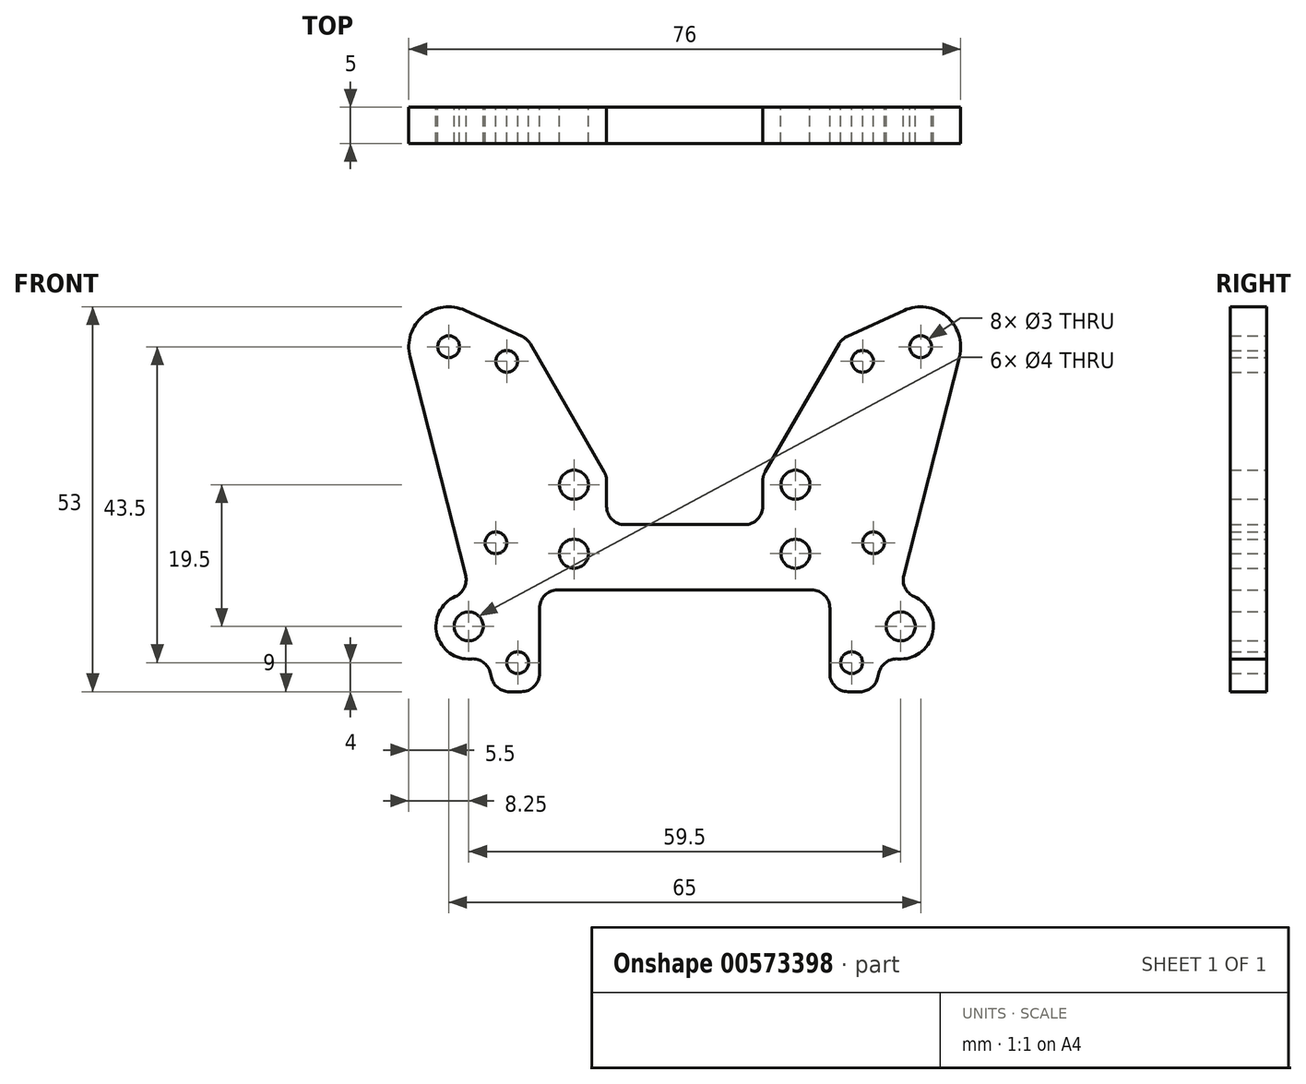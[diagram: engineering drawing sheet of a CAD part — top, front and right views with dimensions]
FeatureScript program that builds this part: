
annotation { "Feature Type Name" : "Feature", "Feature Type Description" : "" }
export const myFeature = defineFeature(function(context is Context, id is Id, definition is map)
    precondition{}
    {
        {
            var Q0;
            Q0=qCreatedBy(makeId("Front.planeOp"),FACE);
            var sketch = newSketch(context, id + "F0", { "sketchPlane" : qUnion([Q0])});
            skLineSegment(sketch, "E0", {"start": v(0, 78.36) * mm, "end": v(0, -63.42) * mm, "construction": true});
            skCircle(sketch, "E1", {"center": v(23, -10) * mm, "radius": 1.5 * mm});
            skCircle(sketch, "E2", {"center": v(29.75, -5) * mm, "radius": 2 * mm});
            skCircle(sketch, "E3", {"center": v(26, 6.5) * mm, "radius": 1.5 * mm});
            skCircle(sketch, "E4", {"center": v(15.25, 5) * mm, "radius": 2 * mm});
            skCircle(sketch, "E5", {"center": v(15.25, 14.5) * mm, "radius": 2 * mm});
            skCircle(sketch, "E6", {"center": v(24.5, 31.5) * mm, "radius": 1.5 * mm});
            skCircle(sketch, "E7", {"center": v(32.5, 33.5) * mm, "radius": 1.5 * mm});
            skLineSegment(sketch, "E8", {"start": v(22.5, -14) * mm, "end": v(24.17, -14) * mm});
            skLineSegment(sketch, "E9", {"start": v(26.59, -12.12) * mm, "end": v(26.78, -11.36) * mm});
            skArc(sketch, "E10.0", {"start": v(29.4, -9.49) * mm, "mid": v(34.11, -6.1) * mm, "end": v(31.58, -0.89) * mm});
            skLineSegment(sketch, "E11.trimOffspring", {"start": v(30.18, 2) * mm, "end": v(37.83, 32.15) * mm});
            skPoint(sketch, "E12.visualSharp", {"position": v(26.11, -14) * mm});
            skArc(sketch, "E12.filletArc", {"start": v(24.17, -14) * mm, "mid": v(25.7, -13.47) * mm, "end": v(26.59, -12.12) * mm});
            skArc(sketch, "E13.0", {"start": v(37.83, 32.15) * mm, "mid": v(36.03, 37.72) * mm, "end": v(30.22, 38.5) * mm});
            skLineSegment(sketch, "E14", {"start": v(30.22, 38.5) * mm, "end": v(22.4, 34.94) * mm});
            skLineSegment(sketch, "E15", {"start": v(10.75, 15.04) * mm, "end": v(10.75, 11.5) * mm});
            skLineSegment(sketch, "E16", {"start": v(8.25, 9) * mm, "end": v(0, 9) * mm});
            skLineSegment(sketch, "E17", {"start": v(0, 9) * mm, "end": v(0, 0) * mm});
            skLineSegment(sketch, "E18", {"start": v(0, 0) * mm, "end": v(17.5, 0) * mm});
            skLineSegment(sketch, "E19", {"start": v(20, -2.5) * mm, "end": v(20, -11.5) * mm});
            skPoint(sketch, "E20.visualSharp", {"position": v(10.75, 29.63) * mm});
            skPoint(sketch, "E21.visualSharp", {"position": v(10.75, 9) * mm});
            skArc(sketch, "E21.filletArc", {"start": v(8.25, 9) * mm, "mid": v(10.02, 9.73) * mm, "end": v(10.75, 11.5) * mm});
            skPoint(sketch, "E22.visualSharp", {"position": v(20, 0) * mm});
            skArc(sketch, "E22.filletArc", {"start": v(20, -2.5) * mm, "mid": v(19.27, -0.73) * mm, "end": v(17.5, 0) * mm});
            skPoint(sketch, "E23.visualSharp", {"position": v(20, -14) * mm});
            skArc(sketch, "E23.filletArc", {"start": v(20, -11.5) * mm, "mid": v(20.73, -13.27) * mm, "end": v(22.5, -14) * mm});
            skLineSegment(sketch, "E24", {"start": v(11.09, 16.29) * mm, "end": v(21.28, 33.92) * mm});
            skPoint(sketch, "E25.visualSharp", {"position": v(21.68, 34.6) * mm});
            skArc(sketch, "E25.filletArc", {"start": v(22.4, 34.94) * mm, "mid": v(21.76, 34.52) * mm, "end": v(21.28, 33.92) * mm});
            skPoint(sketch, "E26.visualSharp", {"position": v(10.75, 15.7) * mm});
            skArc(sketch, "E26.filletArc", {"start": v(11.09, 16.29) * mm, "mid": v(10.84, 15.68) * mm, "end": v(10.75, 15.04) * mm});
            skLineSegment(sketch, "E27", {"start": v(23.2, 32.25) * mm, "end": v(13.52, 15.5) * mm, "construction": true});
            skPoint(sketch, "E28.visualSharp", {"position": v(29.54, -0.5) * mm});
            skArc(sketch, "E28.filletArc", {"start": v(30.18, 2) * mm, "mid": v(30.35, 0.3) * mm, "end": v(31.58, -0.89) * mm});
            skPoint(sketch, "E29.visualSharp", {"position": v(27.42, -8.85) * mm});
            skArc(sketch, "E29.filletArc", {"start": v(29.4, -9.49) * mm, "mid": v(27.75, -9.95) * mm, "end": v(26.78, -11.36) * mm});
            skSolve(sketch);
        }
        {
            var Q0;
            Q0=qSketchRegion(id+"F0",true);
            extrude(context, id + "F1", {"entities" : qUnion([Q0]), "depth" : 5 * mm});
        }
        {
            var Q0;
            Q0=makeQuery(id+"F1.opExtrude","SWEPT_BODY",BODY,{"disambiguationData":[OSD([sQuery(id+"F0.wireOp",EDGE,"E1"),sQuery(id+"F0.wireOp",EDGE,"E2"),sQuery(id+"F0.wireOp",EDGE,"E3"),sQuery(id+"F0.wireOp",EDGE,"E4"),sQuery(id+"F0.wireOp",EDGE,"E5"),sQuery(id+"F0.wireOp",EDGE,"E6"),sQuery(id+"F0.wireOp",EDGE,"E7"),sQuery(id+"F0.wireOp",EDGE,"E8"),sQuery(id+"F0.wireOp",EDGE,"E9"),sQuery(id+"F0.wireOp",EDGE,"E10.0"),sQuery(id+"F0.wireOp",EDGE,"E11.trimOffspring"),sQuery(id+"F0.wireOp",EDGE,"E12.filletArc"),sQuery(id+"F0.wireOp",EDGE,"E13.0"),sQuery(id+"F0.wireOp",EDGE,"E14"),sQuery(id+"F0.wireOp",EDGE,"E15"),sQuery(id+"F0.wireOp",EDGE,"E16"),sQuery(id+"F0.wireOp",EDGE,"E17"),sQuery(id+"F0.wireOp",EDGE,"E18"),sQuery(id+"F0.wireOp",EDGE,"E19"),sQuery(id+"F0.wireOp",EDGE,"E20.filletArc"),sQuery(id+"F0.wireOp",EDGE,"E21.filletArc"),sQuery(id+"F0.wireOp",EDGE,"E22.filletArc"),sQuery(id+"F0.wireOp",EDGE,"E23.filletArc")])]});
            var Q1;
            Q1=qCreatedBy(makeId("Right.planeOp"),FACE);
            mirror(context, id + "F2", {"operationType" : NewBodyOperationType.ADD, "entities" : qUnion([Q0]), "mirrorPlane" : qUnion([Q1])});
        }
    });
